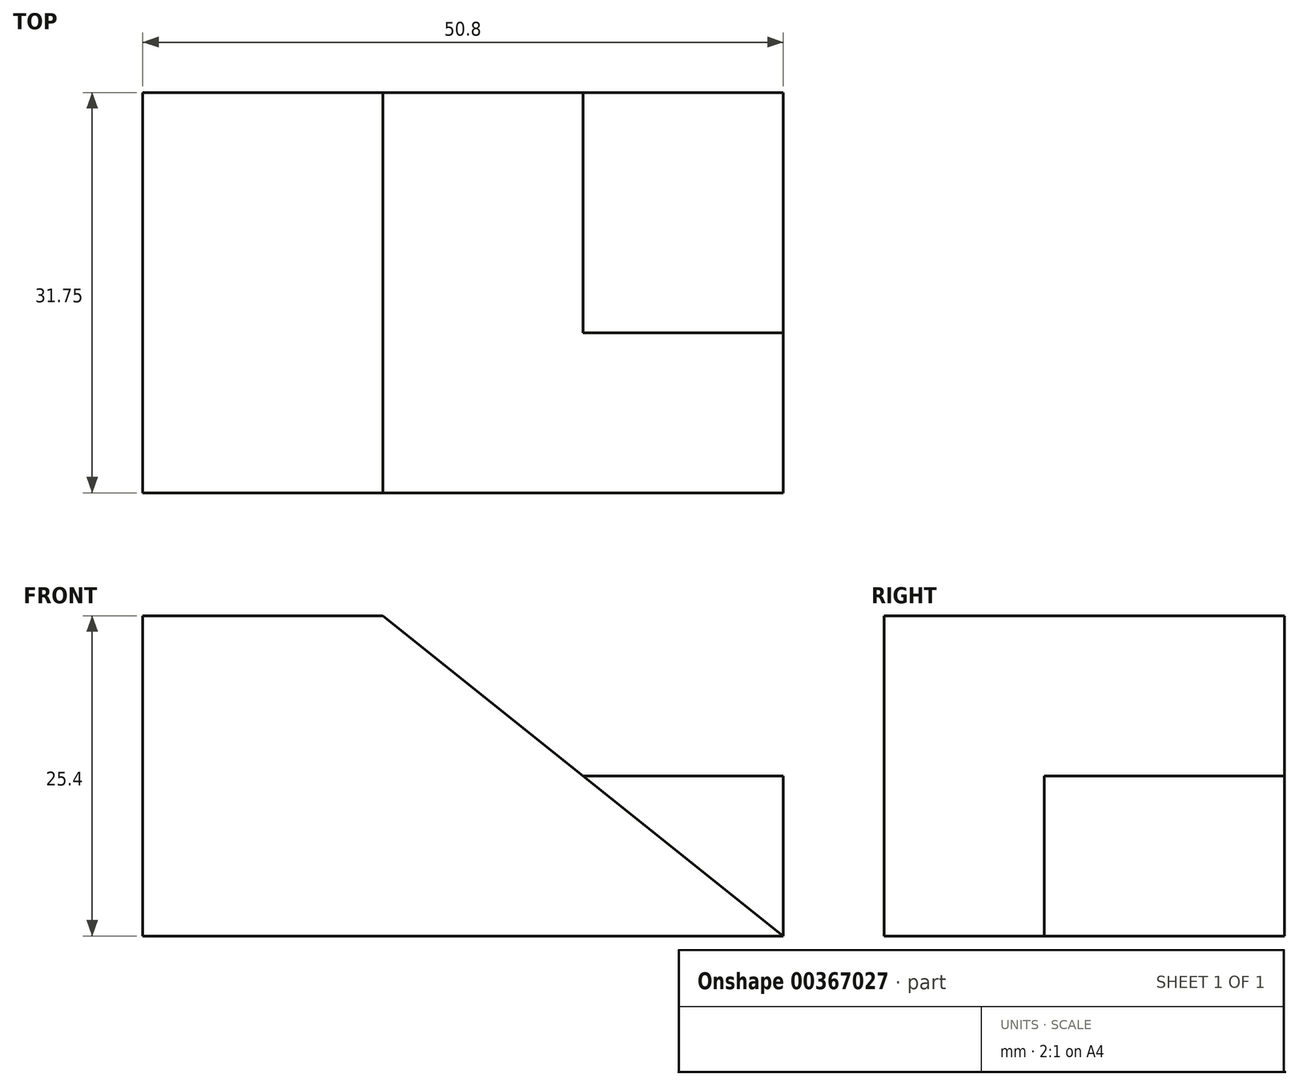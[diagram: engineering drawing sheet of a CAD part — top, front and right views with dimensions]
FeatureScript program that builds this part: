
annotation { "Feature Type Name" : "Feature", "Feature Type Description" : "" }
export const myFeature = defineFeature(function(context is Context, id is Id, definition is map)
    precondition{}
    {
        {
            var Q0;
            Q0=qCreatedBy(makeId("Front.planeOp"),FACE);
            var sketch = newSketch(context, id + "F0", { "sketchPlane" : qUnion([Q0])});
            skLineSegment(sketch, "E0", {"start": v(0, 25.4) * mm, "end": v(0, 0) * mm});
            skLineSegment(sketch, "E1", {"start": v(0, 0) * mm, "end": v(50.8, 0) * mm});
            skLineSegment(sketch, "E2", {"start": v(50.8, 0) * mm, "end": v(50.8, 25.4) * mm});
            skLineSegment(sketch, "E3", {"start": v(50.8, 25.4) * mm, "end": v(0, 25.4) * mm});
            skSolve(sketch);
        }
        {
            var Q0;
            Q0 = qSketchRegion(id + "F0", true);
            extrude(context, id + "F1", {"entities" : qUnion([Q0]), "depth" : 31.75 * mm});
        }
        {
            var Q0;
            Q0=makeQuery(id+"F1.opExtrude","CAP_FACE",FACE,{"disambiguationData":[OSD([sQuery(id+"F0.wireOp",EDGE,"E0"),sQuery(id+"F0.wireOp",EDGE,"E1"),sQuery(id+"F0.wireOp",EDGE,"E2"),sQuery(id+"F0.wireOp",EDGE,"E3")])],"isStart":false});
            var sketch = newSketch(context, id + "F2", { "sketchPlane" : qUnion([Q0])});
            skLineSegment(sketch, "E4", {"start": v(19.05, 25.4) * mm, "end": v(50.8, 0) * mm});
            skSolve(sketch);
        }
        {
            var Q0;
            Q0 = qSketchRegion(id + "F2", true);
            var Q1;
            {var subQ0=sQuery(id+"F2.wireOp",EDGE,"E4");Q1=makeQuery(id+"F2.imprint","IMPRINT",FACE,{"disambiguationData":[TD([[makeQuery(id+"F2.imprint","IMPRINT",EDGE,{"derivedFrom":subQ0}),1.0]])]});}
            extrude(context, id + "F3", {"entities" : qUnion([Q0, Q1]), "operationType" : NewBodyOperationType.REMOVE, "oppositeDirection" : true, "depth" : 12.7 * mm});
        }
        {
            var Q0;
            Q0=makeQuery(id+"F3.boolean.opBoolean","COPY",FACE,{"derivedFrom":makeQuery(id+"F3.opExtrude","CAP_FACE",FACE,{"disambiguationData":[OSD([sQuery(id+"F0.wireOp",EDGE,"E2"),sQuery(id+"F0.wireOp",EDGE,"E3"),sQuery(id+"F2.wireOp",EDGE,"E4")])],"isStart":false})});
            var sketch = newSketch(context, id + "F4", { "sketchPlane" : qUnion([Q0])});
            skLineSegment(sketch, "E5", {"start": v(34.92, 12.7) * mm, "end": v(34.92, 25.4) * mm});
            skSolve(sketch);
        }
        {
            var Q0;
            Q0 = qSketchRegion(id + "F4", true);
            var Q1;
            {var subQ0=sQuery(id+"F4.wireOp",EDGE,"E5");Q1=makeQuery(id+"F4.imprint","IMPRINT",FACE,{"disambiguationData":[TD([[makeQuery(id+"F4.imprint","IMPRINT",EDGE,{"derivedFrom":subQ0}),1.0]])]});}
            extrude(context, id + "F5", {"entities" : qUnion([Q0, Q1]), "operationType" : NewBodyOperationType.REMOVE, "oppositeDirection" : true, "depth" : 25.4 * mm});
        }
        {
            var Q0;
            Q0=makeQuery(id+"F3.boolean.opBoolean","COPY",FACE,{"derivedFrom":makeQuery(id+"F3.opExtrude","CAP_FACE",FACE,{"disambiguationData":[OSD([sQuery(id+"F0.wireOp",EDGE,"E2"),sQuery(id+"F0.wireOp",EDGE,"E3"),sQuery(id+"F2.wireOp",EDGE,"E4")])],"isStart":false})});
            var sketch = newSketch(context, id + "F6", { "sketchPlane" : qUnion([Q0])});
            skLineSegment(sketch, "E6", {"start": v(34.92, 12.7) * mm, "end": v(50.8, 12.7) * mm});
            skSolve(sketch);
        }
        {
            var Q0;
            Q0 = qSketchRegion(id + "F6", true);
            var Q1;
            {var subQ0=sQuery(id+"F6.wireOp",EDGE,"E6");Q1=makeQuery(id+"F6.imprint","IMPRINT",FACE,{"disambiguationData":[TD([[makeQuery(id+"F6.imprint","IMPRINT",EDGE,{"derivedFrom":subQ0}),1.0]])]});}
            extrude(context, id + "F7", {"entities" : qUnion([Q0, Q1]), "operationType" : NewBodyOperationType.REMOVE, "oppositeDirection" : true, "depth" : 25.4 * mm});
        }
    });
